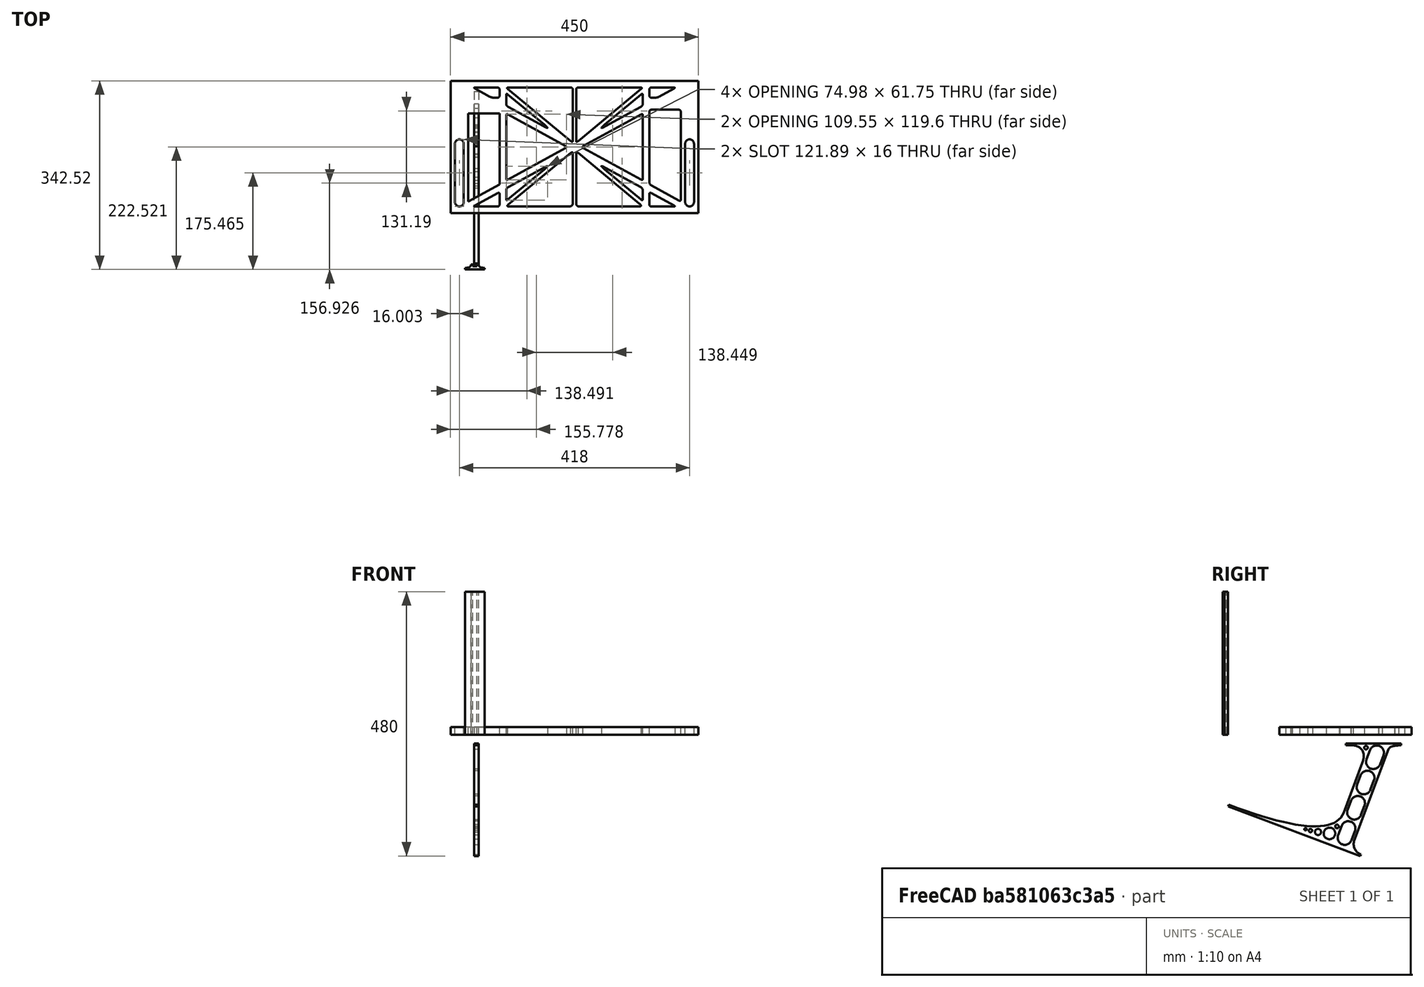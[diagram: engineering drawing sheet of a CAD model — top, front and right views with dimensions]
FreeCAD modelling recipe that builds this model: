
FCSTD DOCUMENT  (FreeCAD 0.19R0.19.2)
Label: laptopStand132FCStd
License: All rights reserved
LicenseURL: http://en.wikipedia.org/wiki/All_rights_reserved
objects: Sketcher::SketchObject×3, Part::Extrusion×3
note: 6 computed .brp shape members not serialized (recipe doc carries the construction recipe); baked Part::Feature solids carry a one-line shape summary decoded from their .brp

FEATURE [Sketcher::SketchObject] Sketch
  FullyConstrained = true
  sketch-geometry (351):
    g0: LineSegment StartX=-10.9272 StartY=-82.7794 StartZ=0 EndX=46.0728 EndY=-51.4823 EndZ=0
    g1: LineSegment StartX=-10.9272 StartY=76.4095 StartZ=0 EndX=-10.9272 EndY=-82.7794 EndZ=0
    g2: LineSegment StartX=46.0728 StartY=76.4095 StartZ=0 EndX=46.0728 EndY=-51.4823 EndZ=0
    g3: LineSegment StartX=-42.9272 StartY=136.221 StartZ=0 EndX=-42.9272 EndY=-103.779 EndZ=0
    g4: LineSegment StartX=407.073 StartY=136.221 StartZ=0 EndX=407.073 EndY=-103.779 EndZ=0
    g5: ArcOfCircle CenterX=-26.9272 CenterY=22.1087 CenterZ=0 NormalX=0 NormalY=0 NormalZ=1 AngleXU=0 Radius=8 StartAngle=1e-16 EndAngle=3.14159
    g6: ArcOfCircle CenterX=-26.9272 CenterY=-83.7794 CenterZ=0 NormalX=0 NormalY=0 NormalZ=1 AngleXU=0 Radius=8 StartAngle=3.14159 EndAngle=6.28319
    g7: LineSegment StartX=-34.9272 StartY=22.1087 StartZ=0 EndX=-34.9272 EndY=-83.7794 EndZ=0
    g8: LineSegment StartX=-18.9272 StartY=22.1087 StartZ=0 EndX=-18.9272 EndY=-83.7794 EndZ=0
    g9: ArcOfCircle CenterX=391.073 CenterY=22.1087 CenterZ=0 NormalX=0 NormalY=0 NormalZ=1 AngleXU=0 Radius=8 StartAngle=-4.4e-15 EndAngle=3.14159
    g10: LineSegment StartX=399.073 StartY=22.1087 StartZ=0 EndX=399.073 EndY=-83.7794 EndZ=0
    g11: LineSegment StartX=383.073 StartY=22.1087 StartZ=0 EndX=383.073 EndY=-83.7794 EndZ=0
    g12: ArcOfCircle CenterX=391.073 CenterY=-83.7794 CenterZ=0 NormalX=0 NormalY=0 NormalZ=1 AngleXU=0 Radius=8 StartAngle=3.14159 EndAngle=6.28319
    g13: Circle CenterX=175.022 CenterY=27.0628 CenterZ=0 NormalX=0 NormalY=0 NormalZ=1 AngleXU=0 Radius=1
    g14: Circle CenterX=179.022 CenterY=24.8665 CenterZ=0 NormalX=0 NormalY=0 NormalZ=1 AngleXU=0 Radius=1
    g15: Circle CenterX=179.022 CenterY=27.0628 CenterZ=0 NormalX=0 NormalY=0 NormalZ=1 AngleXU=0 Radius=1
    g16: BSplineCurve PolesCount=3 KnotsCount=2 Degree=2 IsPeriodic=0
    g17: GeomPoint X=175.022 Y=27.0628 Z=0
    g18: GeomPoint X=179.022 Y=27.0628 Z=0
    g19: Circle CenterX=189.124 CenterY=27.0628 CenterZ=0 NormalX=0 NormalY=0 NormalZ=1 AngleXU=0 Radius=1
    g20: Circle CenterX=185.124 CenterY=24.8665 CenterZ=0 NormalX=0 NormalY=0 NormalZ=1 AngleXU=0 Radius=1
    g21: Circle CenterX=185.124 CenterY=27.0628 CenterZ=0 NormalX=0 NormalY=0 NormalZ=1 AngleXU=0 Radius=1
    g22: BSplineCurve PolesCount=3 KnotsCount=2 Degree=2 IsPeriodic=0
    g23: GeomPoint X=189.124 Y=27.0628 Z=0
    g24: GeomPoint X=185.124 Y=27.0628 Z=0
    g25: Circle CenterX=175.022 CenterY=5.37834 CenterZ=0 NormalX=0 NormalY=0 NormalZ=1 AngleXU=0 Radius=1
    g26: Circle CenterX=179.022 CenterY=7.57463 CenterZ=0 NormalX=0 NormalY=0 NormalZ=1 AngleXU=0 Radius=1
    g27: Circle CenterX=179.022 CenterY=5.34704 CenterZ=0 NormalX=0 NormalY=0 NormalZ=1 AngleXU=0 Radius=1
    g28: BSplineCurve PolesCount=3 KnotsCount=2 Degree=2 IsPeriodic=0
    g29: GeomPoint X=175.022 Y=5.37834 Z=0
    g30: GeomPoint X=179.022 Y=5.34704 Z=0
    g31: Circle CenterX=189.124 CenterY=5.37834 CenterZ=0 NormalX=0 NormalY=0 NormalZ=1 AngleXU=0 Radius=1
    g32: Circle CenterX=185.124 CenterY=7.57463 CenterZ=0 NormalX=0 NormalY=0 NormalZ=1 AngleXU=0 Radius=1
    g33: Circle CenterX=185.124 CenterY=5.34704 CenterZ=0 NormalX=0 NormalY=0 NormalZ=1 AngleXU=0 Radius=1
    g34: BSplineCurve PolesCount=3 KnotsCount=2 Degree=2 IsPeriodic=0
    g35: GeomPoint X=189.124 Y=5.37834 Z=0
    g36: GeomPoint X=185.124 Y=5.34704 Z=0
    g37: Circle CenterX=165.871 CenterY=18.1458 CenterZ=0 NormalX=0 NormalY=0 NormalZ=1 AngleXU=0 Radius=1
    g38: Circle CenterX=169.377 CenterY=16.2206 CenterZ=0 NormalX=0 NormalY=0 NormalZ=1 AngleXU=0 Radius=1
    g39: Circle CenterX=165.871 CenterY=14.2954 CenterZ=0 NormalX=0 NormalY=0 NormalZ=1 AngleXU=0 Radius=1
    g40: BSplineCurve PolesCount=3 KnotsCount=2 Degree=2 IsPeriodic=0
    g41: GeomPoint X=165.871 Y=18.1458 Z=0
    g42: GeomPoint X=165.871 Y=14.2954 Z=0
    g43: Circle CenterX=198.275 CenterY=18.1458 CenterZ=0 NormalX=0 NormalY=0 NormalZ=1 AngleXU=0 Radius=1
    g44: Circle CenterX=194.768 CenterY=16.2206 CenterZ=0 NormalX=0 NormalY=0 NormalZ=1 AngleXU=0 Radius=1
    g45: Circle CenterX=198.275 CenterY=14.2954 CenterZ=0 NormalX=0 NormalY=0 NormalZ=1 AngleXU=0 Radius=1
    g46: BSplineCurve PolesCount=3 KnotsCount=2 Degree=2 IsPeriodic=0
    g47: GeomPoint X=198.275 Y=18.1458 Z=0
    g48: GeomPoint X=198.275 Y=14.2954 Z=0
    g49: LineSegment StartX=407.073 StartY=-103.779 StartZ=0 EndX=-42.9272 EndY=-103.779 EndZ=0
    g50: LineSegment StartX=407.073 StartY=136.221 StartZ=0 EndX=-42.9272 EndY=136.221 EndZ=0
    g51: LineSegment StartX=46.0728 StartY=76.4095 StartZ=0 EndX=-10.9272 EndY=76.4095 EndZ=0
    g52: Circle CenterX=125.607 CenterY=54.1951 CenterZ=0 NormalX=0 NormalY=0 NormalZ=1 AngleXU=0 Radius=1
    g53: Circle CenterX=139.632 CenterY=46.4944 CenterZ=0 NormalX=0 NormalY=0 NormalZ=1 AngleXU=0 Radius=1
    g54: Circle CenterX=127.326 CenterY=56.7187 CenterZ=0 NormalX=0 NormalY=0 NormalZ=1 AngleXU=0 Radius=1
    g55: BSplineCurve PolesCount=3 KnotsCount=2 Degree=2 IsPeriodic=0
    g56: GeomPoint X=125.607 Y=54.1951 Z=0
    g57: GeomPoint X=127.326 Y=56.7187 Z=0
    g58: Circle CenterX=236.821 CenterY=56.7187 CenterZ=0 NormalX=0 NormalY=0 NormalZ=1 AngleXU=0 Radius=1
    g59: Circle CenterX=224.513 CenterY=46.4944 CenterZ=0 NormalX=0 NormalY=0 NormalZ=1 AngleXU=0 Radius=1
    g60: Circle CenterX=238.538 CenterY=54.1951 CenterZ=0 NormalX=0 NormalY=0 NormalZ=1 AngleXU=0 Radius=1
    g61: BSplineCurve PolesCount=3 KnotsCount=2 Degree=2 IsPeriodic=0
    g62: GeomPoint X=236.821 Y=56.7187 Z=0
    g63: GeomPoint X=238.538 Y=54.1951 Z=0
    g64: Circle CenterX=238.538 CenterY=-21.7539 CenterZ=0 NormalX=0 NormalY=0 NormalZ=1 AngleXU=0 Radius=1
    g65: Circle CenterX=224.513 CenterY=-14.0532 CenterZ=0 NormalX=0 NormalY=0 NormalZ=1 AngleXU=0 Radius=1
    g66: Circle CenterX=236.821 CenterY=-24.2775 CenterZ=0 NormalX=0 NormalY=0 NormalZ=1 AngleXU=0 Radius=1
    g67: BSplineCurve PolesCount=3 KnotsCount=2 Degree=2 IsPeriodic=0
    g68: GeomPoint X=238.538 Y=-21.7539 Z=0
    g69: GeomPoint X=236.821 Y=-24.2775 Z=0
    g70: Circle CenterX=125.607 CenterY=-21.7539 CenterZ=0 NormalX=0 NormalY=0 NormalZ=1 AngleXU=0 Radius=1
    g71: Circle CenterX=139.632 CenterY=-14.0532 CenterZ=0 NormalX=0 NormalY=0 NormalZ=1 AngleXU=0 Radius=1
    g72: Circle CenterX=127.325 CenterY=-24.2775 CenterZ=0 NormalX=0 NormalY=0 NormalZ=1 AngleXU=0 Radius=1
    g73: BSplineCurve PolesCount=3 KnotsCount=2 Degree=2 IsPeriodic=0
    g74: GeomPoint X=125.607 Y=-21.7539 Z=0
    g75: GeomPoint X=127.325 Y=-24.2775 Z=0
    g76: Circle CenterX=302.996 CenterY=111.695 CenterZ=0 NormalX=0 NormalY=0 NormalZ=1 AngleXU=0 Radius=1
    g77: Circle CenterX=306.073 CenterY=114.251 CenterZ=0 NormalX=0 NormalY=0 NormalZ=1 AngleXU=0 Radius=1
    g78: Circle CenterX=306.073 CenterY=110.251 CenterZ=0 NormalX=0 NormalY=0 NormalZ=1 AngleXU=0 Radius=1
    g79: BSplineCurve PolesCount=3 KnotsCount=2 Degree=2 IsPeriodic=0
    g80: GeomPoint X=302.996 Y=111.695 Z=0
    g81: GeomPoint X=306.073 Y=110.251 Z=0
    g82: Circle CenterX=306.073 CenterY=95.2763 CenterZ=0 NormalX=0 NormalY=0 NormalZ=1 AngleXU=0 Radius=1
    g83: Circle CenterX=306.073 CenterY=91.2763 CenterZ=0 NormalX=0 NormalY=0 NormalZ=1 AngleXU=0 Radius=1
    g84: Circle CenterX=302.567 CenterY=89.3511 CenterZ=0 NormalX=0 NormalY=0 NormalZ=1 AngleXU=0 Radius=1
    g85: BSplineCurve PolesCount=3 KnotsCount=2 Degree=2 IsPeriodic=0
    g86: GeomPoint X=306.073 Y=95.2763 Z=0
    g87: GeomPoint X=302.567 Y=89.3511 Z=0
    g88: LineSegment StartX=306.073 StartY=110.251 StartZ=0 EndX=306.073 EndY=95.2763 EndZ=0
    g89: LineSegment StartX=302.996 StartY=111.695 StartZ=0 EndX=236.821 EndY=56.7187 EndZ=0
    g90: LineSegment StartX=238.538 StartY=54.1951 StartZ=0 EndX=302.567 EndY=89.3511 EndZ=0
    g91: Circle CenterX=61.1496 CenterY=111.695 CenterZ=0 NormalX=0 NormalY=0 NormalZ=1 AngleXU=0 Radius=1
    g92: Circle CenterX=58.0728 CenterY=114.251 CenterZ=0 NormalX=0 NormalY=0 NormalZ=1 AngleXU=0 Radius=1
    g93: Circle CenterX=58.0728 CenterY=110.251 CenterZ=0 NormalX=0 NormalY=0 NormalZ=1 AngleXU=0 Radius=1
    g94: BSplineCurve PolesCount=3 KnotsCount=2 Degree=2 IsPeriodic=0
    g95: GeomPoint X=61.1496 Y=111.695 Z=0
    g96: GeomPoint X=58.0728 Y=110.251 Z=0
    g97: Circle CenterX=61.5791 CenterY=89.3511 CenterZ=0 NormalX=0 NormalY=0 NormalZ=1 AngleXU=0 Radius=1
    g98: Circle CenterX=58.0728 CenterY=91.2763 CenterZ=0 NormalX=0 NormalY=0 NormalZ=1 AngleXU=0 Radius=1
    g99: Circle CenterX=58.0728 CenterY=95.2763 CenterZ=0 NormalX=0 NormalY=0 NormalZ=1 AngleXU=0 Radius=1
    g100: BSplineCurve PolesCount=3 KnotsCount=2 Degree=2 IsPeriodic=0
    g101: GeomPoint X=61.5791 Y=89.3511 Z=0
    g102: GeomPoint X=58.0728 Y=95.2763 Z=0
    g103: LineSegment StartX=58.0728 StartY=110.251 StartZ=0 EndX=58.0728 EndY=95.2763 EndZ=0
    g104: LineSegment StartX=61.1496 StartY=111.695 StartZ=0 EndX=127.326 EndY=56.7187 EndZ=0
    g105: LineSegment StartX=125.607 StartY=54.1951 StartZ=0 EndX=61.5791 EndY=89.3511 EndZ=0
    g106: Circle CenterX=61.5791 CenterY=-56.9099 CenterZ=0 NormalX=0 NormalY=0 NormalZ=1 AngleXU=0 Radius=1
    g107: Circle CenterX=58.0728 CenterY=-58.8351 CenterZ=0 NormalX=0 NormalY=0 NormalZ=1 AngleXU=0 Radius=1
    g108: Circle CenterX=58.0728 CenterY=-62.8351 CenterZ=0 NormalX=0 NormalY=0 NormalZ=1 AngleXU=0 Radius=1
    g109: BSplineCurve PolesCount=3 KnotsCount=2 Degree=2 IsPeriodic=0
    g110: GeomPoint X=61.5791 Y=-56.9099 Z=0
    g111: GeomPoint X=58.0728 Y=-62.8351 Z=0
    g112: Circle CenterX=58.0728 CenterY=-77.8102 CenterZ=0 NormalX=0 NormalY=0 NormalZ=1 AngleXU=0 Radius=1
    g113: Circle CenterX=58.0728 CenterY=-81.8102 CenterZ=0 NormalX=0 NormalY=0 NormalZ=1 AngleXU=0 Radius=1
    g114: Circle CenterX=61.1496 CenterY=-79.2541 CenterZ=0 NormalX=0 NormalY=0 NormalZ=1 AngleXU=0 Radius=1
    g115: BSplineCurve PolesCount=3 KnotsCount=2 Degree=2 IsPeriodic=0
    g116: GeomPoint X=58.0728 Y=-77.8102 Z=0
    g117: GeomPoint X=61.1496 Y=-79.2541 Z=0
    g118: LineSegment StartX=58.0728 StartY=-62.8351 StartZ=0 EndX=58.0728 EndY=-77.8102 EndZ=0
    g119: LineSegment StartX=61.1496 StartY=-79.2541 StartZ=0 EndX=127.325 EndY=-24.2775 EndZ=0
    g120: LineSegment StartX=125.607 StartY=-21.7539 StartZ=0 EndX=61.5791 EndY=-56.9099 EndZ=0
    g121: Circle CenterX=302.567 CenterY=-56.9099 CenterZ=0 NormalX=0 NormalY=0 NormalZ=1 AngleXU=0 Radius=1
    g122: Circle CenterX=306.073 CenterY=-58.8351 CenterZ=0 NormalX=0 NormalY=0 NormalZ=1 AngleXU=0 Radius=1
    g123: Circle CenterX=306.073 CenterY=-62.8351 CenterZ=0 NormalX=0 NormalY=0 NormalZ=1 AngleXU=0 Radius=1
    g124: BSplineCurve PolesCount=3 KnotsCount=2 Degree=2 IsPeriodic=0
    g125: GeomPoint X=302.567 Y=-56.9099 Z=0
    g126: GeomPoint X=306.073 Y=-62.8351 Z=0
    g127: Circle CenterX=302.996 CenterY=-79.2541 CenterZ=0 NormalX=0 NormalY=0 NormalZ=1 AngleXU=0 Radius=1
    g128: Circle CenterX=306.073 CenterY=-81.8102 CenterZ=0 NormalX=0 NormalY=0 NormalZ=1 AngleXU=0 Radius=1
    g129: Circle CenterX=306.073 CenterY=-77.8102 CenterZ=0 NormalX=0 NormalY=0 NormalZ=1 AngleXU=0 Radius=1
    g130: BSplineCurve PolesCount=3 KnotsCount=2 Degree=2 IsPeriodic=0
    g131: GeomPoint X=302.996 Y=-79.2541 Z=0
    g132: GeomPoint X=306.073 Y=-77.8102 Z=0
    g133: LineSegment StartX=306.073 StartY=-62.8351 StartZ=0 EndX=306.073 EndY=-77.8102 EndZ=0
    g134: LineSegment StartX=302.996 StartY=-79.2541 StartZ=0 EndX=236.821 EndY=-24.2775 EndZ=0
    g135: LineSegment StartX=238.538 StartY=-21.7539 StartZ=0 EndX=302.567 EndY=-56.9099 EndZ=0
    g136: Circle CenterX=61.6457 CenterY=-88.8112 CenterZ=0 NormalX=0 NormalY=0 NormalZ=1 AngleXU=0 Radius=1
    g137: Circle CenterX=58.0728 CenterY=-91.7794 CenterZ=0 NormalX=0 NormalY=0 NormalZ=1 AngleXU=0 Radius=1
    g138: Circle CenterX=63.9135 CenterY=-91.7794 CenterZ=0 NormalX=0 NormalY=0 NormalZ=1 AngleXU=0 Radius=1
    g139: BSplineCurve PolesCount=3 KnotsCount=2 Degree=2 IsPeriodic=0
    g140: GeomPoint X=61.6457 Y=-88.8112 Z=0
    g141: GeomPoint X=63.9135 Y=-91.7794 Z=0
    g142: Circle CenterX=179.022 CenterY=-85.8163 CenterZ=0 NormalX=0 NormalY=0 NormalZ=1 AngleXU=0 Radius=1
    g143: Circle CenterX=179.022 CenterY=-91.7794 CenterZ=0 NormalX=0 NormalY=0 NormalZ=1 AngleXU=0 Radius=1
    g144: Circle CenterX=171.895 CenterY=-91.7794 CenterZ=0 NormalX=0 NormalY=0 NormalZ=1 AngleXU=0 Radius=1
    g145: BSplineCurve PolesCount=3 KnotsCount=2 Degree=2 IsPeriodic=0
    g146: GeomPoint X=179.022 Y=-85.8163 Z=0
    g147: GeomPoint X=171.895 Y=-91.7794 Z=0
    g148: Circle CenterX=185.124 CenterY=-86.2028 CenterZ=0 NormalX=0 NormalY=0 NormalZ=1 AngleXU=0 Radius=1
    g149: Circle CenterX=185.124 CenterY=-91.7794 CenterZ=0 NormalX=0 NormalY=0 NormalZ=1 AngleXU=0 Radius=1
    g150: Circle CenterX=191.747 CenterY=-91.7794 CenterZ=0 NormalX=0 NormalY=0 NormalZ=1 AngleXU=0 Radius=1
    g151: BSplineCurve PolesCount=3 KnotsCount=2 Degree=2 IsPeriodic=0
    g152: GeomPoint X=185.124 Y=-86.2028 Z=0
    g153: GeomPoint X=191.747 Y=-91.7794 Z=0
    g154: Circle CenterX=299.888 CenterY=-86.6413 CenterZ=0 NormalX=0 NormalY=0 NormalZ=1 AngleXU=0 Radius=1
    g155: Circle CenterX=306.073 CenterY=-91.7794 CenterZ=0 NormalX=0 NormalY=0 NormalZ=1 AngleXU=0 Radius=1
    g156: Circle CenterX=298.776 CenterY=-91.7794 CenterZ=0 NormalX=0 NormalY=0 NormalZ=1 AngleXU=0 Radius=1
    g157: BSplineCurve PolesCount=3 KnotsCount=2 Degree=2 IsPeriodic=0
    g158: GeomPoint X=299.888 Y=-86.6413 Z=0
    g159: GeomPoint X=298.776 Y=-91.7794 Z=0
    g160: LineSegment StartX=189.124 StartY=5.37834 StartZ=0 EndX=299.888 EndY=-86.6413 EndZ=0
    g161: LineSegment StartX=298.776 StartY=-91.7794 StartZ=0 EndX=191.747 EndY=-91.7794 EndZ=0
    g162: LineSegment StartX=185.124 StartY=-86.2028 StartZ=0 EndX=185.124 EndY=5.34704 EndZ=0
    g163: LineSegment StartX=179.022 StartY=5.34704 StartZ=0 EndX=179.022 EndY=-85.8163 EndZ=0
    g164: LineSegment StartX=171.895 StartY=-91.7794 StartZ=0 EndX=63.9135 EndY=-91.7794 EndZ=0
    g165: LineSegment StartX=61.6457 StartY=-88.8112 StartZ=0 EndX=175.022 EndY=5.37834 EndZ=0
    g166: Circle CenterX=302.073 CenterY=124.221 CenterZ=0 NormalX=0 NormalY=0 NormalZ=1 AngleXU=0 Radius=1
    g167: Circle CenterX=306.073 CenterY=124.221 CenterZ=0 NormalX=0 NormalY=0 NormalZ=1 AngleXU=0 Radius=1
    g168: Circle CenterX=302.996 CenterY=121.665 CenterZ=0 NormalX=0 NormalY=0 NormalZ=1 AngleXU=0 Radius=1
    g169: BSplineCurve PolesCount=3 KnotsCount=2 Degree=2 IsPeriodic=0
    g170: GeomPoint X=302.073 Y=124.221 Z=0
    g171: GeomPoint X=302.996 Y=121.665 Z=0
    g172: Circle CenterX=189.124 CenterY=124.221 CenterZ=0 NormalX=0 NormalY=0 NormalZ=1 AngleXU=0 Radius=1
    g173: Circle CenterX=185.124 CenterY=124.221 CenterZ=0 NormalX=0 NormalY=0 NormalZ=1 AngleXU=0 Radius=1
    g174: Circle CenterX=185.124 CenterY=120.221 CenterZ=0 NormalX=0 NormalY=0 NormalZ=1 AngleXU=0 Radius=1
    g175: BSplineCurve PolesCount=3 KnotsCount=2 Degree=2 IsPeriodic=0
    g176: GeomPoint X=189.124 Y=124.221 Z=0
    g177: GeomPoint X=185.124 Y=120.221 Z=0
    g178: Circle CenterX=175.022 CenterY=124.221 CenterZ=0 NormalX=0 NormalY=0 NormalZ=1 AngleXU=0 Radius=1
    g179: Circle CenterX=179.022 CenterY=124.221 CenterZ=0 NormalX=0 NormalY=0 NormalZ=1 AngleXU=0 Radius=1
    g180: Circle CenterX=179.022 CenterY=120.221 CenterZ=0 NormalX=0 NormalY=0 NormalZ=1 AngleXU=0 Radius=1
    g181: BSplineCurve PolesCount=3 KnotsCount=2 Degree=2 IsPeriodic=0
    g182: GeomPoint X=175.022 Y=124.221 Z=0
    g183: GeomPoint X=179.022 Y=120.221 Z=0
    g184: Circle CenterX=62.0728 CenterY=124.221 CenterZ=0 NormalX=0 NormalY=0 NormalZ=1 AngleXU=0 Radius=1
    g185: Circle CenterX=58.0728 CenterY=124.221 CenterZ=0 NormalX=0 NormalY=0 NormalZ=1 AngleXU=0 Radius=1
    g186: Circle CenterX=61.1496 CenterY=121.665 CenterZ=0 NormalX=0 NormalY=0 NormalZ=1 AngleXU=0 Radius=1
    g187: BSplineCurve PolesCount=3 KnotsCount=2 Degree=2 IsPeriodic=0
    g188: GeomPoint X=62.0728 Y=124.221 Z=0
    g189: GeomPoint X=61.1496 Y=121.665 Z=0
    g190: LineSegment StartX=62.0728 StartY=124.221 StartZ=0 EndX=175.022 EndY=124.221 EndZ=0
    g191: LineSegment StartX=179.022 StartY=120.221 StartZ=0 EndX=179.022 EndY=27.0628 EndZ=0
    g192: LineSegment StartX=185.124 StartY=27.0628 StartZ=0 EndX=185.124 EndY=120.221 EndZ=0
    g193: LineSegment StartX=189.124 StartY=124.221 StartZ=0 EndX=302.073 EndY=124.221 EndZ=0
    g194: LineSegment StartX=302.996 StartY=121.665 StartZ=0 EndX=189.124 EndY=27.0628 EndZ=0
    g195: LineSegment StartX=175.022 StartY=27.0628 StartZ=0 EndX=61.1496 EndY=121.665 EndZ=0
    g196: Circle CenterX=61.5791 CenterY=75.4095 CenterZ=0 NormalX=0 NormalY=0 NormalZ=1 AngleXU=0 Radius=1
    g197: Circle CenterX=58.0728 CenterY=77.3346 CenterZ=0 NormalX=0 NormalY=0 NormalZ=1 AngleXU=0 Radius=1
    g198: Circle CenterX=58.0728 CenterY=73.3346 CenterZ=0 NormalX=0 NormalY=0 NormalZ=1 AngleXU=0 Radius=1
    g199: BSplineCurve PolesCount=3 KnotsCount=2 Degree=2 IsPeriodic=0
    g200: GeomPoint X=61.5791 Y=75.4095 Z=0
    g201: GeomPoint X=58.0728 Y=73.3346 Z=0
    g202: Circle CenterX=58.0728 CenterY=-40.8935 CenterZ=0 NormalX=0 NormalY=0 NormalZ=1 AngleXU=0 Radius=1
    g203: Circle CenterX=58.0728 CenterY=-44.8935 CenterZ=0 NormalX=0 NormalY=0 NormalZ=1 AngleXU=0 Radius=1
    g204: Circle CenterX=61.5791 CenterY=-42.9683 CenterZ=0 NormalX=0 NormalY=0 NormalZ=1 AngleXU=0 Radius=1
    g205: BSplineCurve PolesCount=3 KnotsCount=2 Degree=2 IsPeriodic=0
    g206: GeomPoint X=58.0728 Y=-40.8935 Z=0
    g207: GeomPoint X=61.5791 Y=-42.9683 Z=0
    g208: LineSegment StartX=61.5791 StartY=-42.9683 StartZ=0 EndX=165.871 EndY=14.2954 EndZ=0
    g209: LineSegment StartX=165.871 StartY=18.1458 StartZ=0 EndX=61.5791 EndY=75.4095 EndZ=0
    g210: LineSegment StartX=58.0728 StartY=73.3346 StartZ=0 EndX=58.0728 EndY=-40.8935 EndZ=0
    g211: Circle CenterX=302.567 CenterY=-42.9683 CenterZ=0 NormalX=0 NormalY=0 NormalZ=1 AngleXU=0 Radius=1
    g212: Circle CenterX=306.073 CenterY=-44.8935 CenterZ=0 NormalX=0 NormalY=0 NormalZ=1 AngleXU=0 Radius=1
    g213: Circle CenterX=306.073 CenterY=-40.8935 CenterZ=0 NormalX=0 NormalY=0 NormalZ=1 AngleXU=0 Radius=1
    g214: BSplineCurve PolesCount=3 KnotsCount=2 Degree=2 IsPeriodic=0
    g215: GeomPoint X=302.567 Y=-42.9683 Z=0
    g216: GeomPoint X=306.073 Y=-40.8935 Z=0
    g217: Circle CenterX=306.073 CenterY=73.3346 CenterZ=0 NormalX=0 NormalY=0 NormalZ=1 AngleXU=0 Radius=1
    g218: Circle CenterX=306.073 CenterY=77.3346 CenterZ=0 NormalX=0 NormalY=0 NormalZ=1 AngleXU=0 Radius=1
    g219: Circle CenterX=302.567 CenterY=75.4095 CenterZ=0 NormalX=0 NormalY=0 NormalZ=1 AngleXU=0 Radius=1
    g220: BSplineCurve PolesCount=3 KnotsCount=2 Degree=2 IsPeriodic=0
    g221: GeomPoint X=306.073 Y=73.3346 Z=0
    g222: GeomPoint X=302.567 Y=75.4095 Z=0
    g223: LineSegment StartX=302.567 StartY=-42.9683 StartZ=0 EndX=198.275 EndY=14.2954 EndZ=0
    g224: LineSegment StartX=198.275 StartY=18.1458 StartZ=0 EndX=302.567 EndY=75.4095 EndZ=0
    g225: LineSegment StartX=306.073 StartY=73.3346 StartZ=0 EndX=306.073 EndY=-40.8935 EndZ=0
    g226: LineSegment StartX=322.073 StartY=105.865 StartZ=0 EndX=328.643 EndY=105.865 EndZ=0
    g227: LineSegment StartX=318.073 StartY=120.221 StartZ=0 EndX=318.073 EndY=109.865 EndZ=0
    g228: LineSegment StartX=336.157 StartY=107.779 StartZ=0 EndX=362.567 EndY=122.294 EndZ=0
    g229: Circle CenterX=362.073 CenterY=124.221 CenterZ=0 NormalX=0 NormalY=0 NormalZ=1 AngleXU=0 Radius=1
    g230: Circle CenterX=366.073 CenterY=124.221 CenterZ=0 NormalX=0 NormalY=0 NormalZ=1 AngleXU=0 Radius=1
    g231: Circle CenterX=362.567 CenterY=122.294 CenterZ=0 NormalX=0 NormalY=0 NormalZ=1 AngleXU=0 Radius=1
    g232: BSplineCurve PolesCount=3 KnotsCount=2 Degree=2 IsPeriodic=0
    g233: GeomPoint X=362.073 Y=124.221 Z=0
    g234: GeomPoint X=362.567 Y=122.294 Z=0
    g235: Circle CenterX=322.073 CenterY=124.221 CenterZ=0 NormalX=0 NormalY=0 NormalZ=1 AngleXU=0 Radius=1
    g236: Circle CenterX=318.073 CenterY=124.221 CenterZ=0 NormalX=0 NormalY=0 NormalZ=1 AngleXU=0 Radius=1
    g237: Circle CenterX=318.073 CenterY=120.221 CenterZ=0 NormalX=0 NormalY=0 NormalZ=1 AngleXU=0 Radius=1
    g238: BSplineCurve PolesCount=3 KnotsCount=2 Degree=2 IsPeriodic=0
    g239: GeomPoint X=322.073 Y=124.221 Z=0
    g240: GeomPoint X=318.073 Y=120.221 Z=0
    g241: Circle CenterX=322.073 CenterY=105.865 CenterZ=0 NormalX=0 NormalY=0 NormalZ=1 AngleXU=0 Radius=1
    g242: Circle CenterX=318.073 CenterY=105.865 CenterZ=0 NormalX=0 NormalY=0 NormalZ=1 AngleXU=0 Radius=1
    g243: Circle CenterX=318.073 CenterY=109.865 CenterZ=0 NormalX=0 NormalY=0 NormalZ=1 AngleXU=0 Radius=1
    g244: BSplineCurve PolesCount=3 KnotsCount=2 Degree=2 IsPeriodic=0
    g245: GeomPoint X=322.073 Y=105.865 Z=0
    g246: GeomPoint X=318.073 Y=109.865 Z=0
    g247: Circle CenterX=336.157 CenterY=107.779 CenterZ=0 NormalX=0 NormalY=0 NormalZ=1 AngleXU=0 Radius=1
    g248: Circle CenterX=332.651 CenterY=105.853 CenterZ=0 NormalX=0 NormalY=0 NormalZ=1 AngleXU=0 Radius=1
    g249: Circle CenterX=328.643 CenterY=105.865 CenterZ=0 NormalX=0 NormalY=0 NormalZ=1 AngleXU=0 Radius=1
    g250: BSplineCurve PolesCount=3 KnotsCount=2 Degree=2 IsPeriodic=0
    g251: GeomPoint X=336.157 Y=107.779 Z=0
    g252: GeomPoint X=328.643 Y=105.865 Z=0
    g253: LineSegment StartX=322.073 StartY=124.221 StartZ=0 EndX=362.073 EndY=124.221 EndZ=0
    g254: Circle CenterX=371.567 CenterY=-80.8644 CenterZ=0 NormalX=0 NormalY=0 NormalZ=1 AngleXU=0 Radius=1
    g255: Circle CenterX=375.073 CenterY=-82.7896 CenterZ=0 NormalX=0 NormalY=0 NormalZ=1 AngleXU=0 Radius=1
    g256: Circle CenterX=375.073 CenterY=-78.7896 CenterZ=0 NormalX=0 NormalY=0 NormalZ=1 AngleXU=0 Radius=1
    g257: BSplineCurve PolesCount=3 KnotsCount=2 Degree=2 IsPeriodic=0
    g258: GeomPoint X=371.567 Y=-80.8644 Z=0
    g259: GeomPoint X=375.073 Y=-78.7896 Z=0
    g260: Circle CenterX=321.579 CenterY=-53.4075 CenterZ=0 NormalX=0 NormalY=0 NormalZ=1 AngleXU=0 Radius=1
    g261: Circle CenterX=318.073 CenterY=-51.4823 CenterZ=0 NormalX=0 NormalY=0 NormalZ=1 AngleXU=0 Radius=1
    g262: Circle CenterX=318.073 CenterY=-47.4823 CenterZ=0 NormalX=0 NormalY=0 NormalZ=1 AngleXU=0 Radius=1
    g263: BSplineCurve PolesCount=3 KnotsCount=2 Degree=2 IsPeriodic=0
    g264: GeomPoint X=321.579 Y=-53.4075 Z=0
    g265: GeomPoint X=318.073 Y=-47.4823 Z=0
    g266: LineSegment StartX=371.567 StartY=-80.8644 StartZ=0 EndX=321.579 EndY=-53.4075 EndZ=0
    g267: LineSegment StartX=318.073 StartY=-47.4823 StartZ=0 EndX=318.073 EndY=76.4095 EndZ=0
    g268: Circle CenterX=321.579 CenterY=-67.3492 CenterZ=0 NormalX=0 NormalY=0 NormalZ=1 AngleXU=0 Radius=1
    g269: Circle CenterX=318.073 CenterY=-65.424 CenterZ=0 NormalX=0 NormalY=0 NormalZ=1 AngleXU=0 Radius=1
    g270: Circle CenterX=318.073 CenterY=-69.424 CenterZ=0 NormalX=0 NormalY=0 NormalZ=1 AngleXU=0 Radius=1
    g271: BSplineCurve PolesCount=3 KnotsCount=2 Degree=2 IsPeriodic=0
    g272: GeomPoint X=321.579 Y=-67.3492 Z=0
    g273: GeomPoint X=318.073 Y=-69.424 Z=0
    g274: Circle CenterX=362.567 CenterY=-89.8542 CenterZ=0 NormalX=0 NormalY=0 NormalZ=1 AngleXU=0 Radius=1
    g275: Circle CenterX=366.073 CenterY=-91.7794 CenterZ=0 NormalX=0 NormalY=0 NormalZ=1 AngleXU=0 Radius=1
    g276: Circle CenterX=362.073 CenterY=-91.7794 CenterZ=0 NormalX=0 NormalY=0 NormalZ=1 AngleXU=0 Radius=1
    g277: BSplineCurve PolesCount=3 KnotsCount=2 Degree=2 IsPeriodic=0
    g278: GeomPoint X=362.567 Y=-89.8542 Z=0
    g279: GeomPoint X=362.073 Y=-91.7794 Z=0
    g280: Circle CenterX=322.073 CenterY=-91.7794 CenterZ=0 NormalX=0 NormalY=0 NormalZ=1 AngleXU=0 Radius=1
    g281: Circle CenterX=318.073 CenterY=-91.7794 CenterZ=0 NormalX=0 NormalY=0 NormalZ=1 AngleXU=0 Radius=1
    g282: Circle CenterX=318.073 CenterY=-87.7794 CenterZ=0 NormalX=0 NormalY=0 NormalZ=1 AngleXU=0 Radius=1
    g283: BSplineCurve PolesCount=3 KnotsCount=2 Degree=2 IsPeriodic=0
    g284: GeomPoint X=322.073 Y=-91.7794 Z=0
    g285: GeomPoint X=318.073 Y=-87.7794 Z=0
    g286: LineSegment StartX=362.567 StartY=-89.8542 StartZ=0 EndX=321.579 EndY=-67.3492 EndZ=0
    g287: LineSegment StartX=318.073 StartY=-69.424 StartZ=0 EndX=318.073 EndY=-87.7794 EndZ=0
    g288: LineSegment StartX=322.073 StartY=-91.7794 StartZ=0 EndX=362.073 EndY=-91.7794 EndZ=0
    g289: Circle CenterX=2.07281 CenterY=124.221 CenterZ=0 NormalX=0 NormalY=0 NormalZ=1 AngleXU=0 Radius=1
    g290: Circle CenterX=1.57905 CenterY=122.295 CenterZ=0 NormalX=0 NormalY=0 NormalZ=1 AngleXU=0 Radius=1
    g291: BSplineCurve PolesCount=3 KnotsCount=2 Degree=2 IsPeriodic=0
    g292: GeomPoint X=2.07281 Y=124.221 Z=0
    g293: GeomPoint X=1.57905 Y=122.295 Z=0
    g294: Circle CenterX=42.0728 CenterY=124.221 CenterZ=0 NormalX=0 NormalY=0 NormalZ=1 AngleXU=0 Radius=1
    g295: Circle CenterX=46.0728 CenterY=124.221 CenterZ=0 NormalX=0 NormalY=0 NormalZ=1 AngleXU=0 Radius=1
    g296: Circle CenterX=46.0728 CenterY=120.221 CenterZ=0 NormalX=0 NormalY=0 NormalZ=1 AngleXU=0 Radius=1
    g297: BSplineCurve PolesCount=3 KnotsCount=2 Degree=2 IsPeriodic=0
    g298: GeomPoint X=42.0728 Y=124.221 Z=0
    g299: GeomPoint X=46.0728 Y=120.221 Z=0
    g300: Circle CenterX=46.0728 CenterY=109.865 CenterZ=0 NormalX=0 NormalY=0 NormalZ=1 AngleXU=0 Radius=1
    g301: Circle CenterX=46.0728 CenterY=105.865 CenterZ=0 NormalX=0 NormalY=0 NormalZ=1 AngleXU=0 Radius=1
    g302: Circle CenterX=42.0728 CenterY=105.865 CenterZ=0 NormalX=0 NormalY=0 NormalZ=1 AngleXU=0 Radius=1
    g303: BSplineCurve PolesCount=3 KnotsCount=2 Degree=2 IsPeriodic=0
    g304: GeomPoint X=46.0728 Y=109.865 Z=0
    g305: GeomPoint X=42.0728 Y=105.865 Z=0
    g306: Circle CenterX=35.5028 CenterY=105.865 CenterZ=0 NormalX=0 NormalY=0 NormalZ=1 AngleXU=0 Radius=1
    g307: Circle CenterX=31.5028 CenterY=105.865 CenterZ=0 NormalX=0 NormalY=0 NormalZ=1 AngleXU=0 Radius=1
    g308: Circle CenterX=27.9965 CenterY=107.79 CenterZ=0 NormalX=0 NormalY=0 NormalZ=1 AngleXU=0 Radius=1
    g309: BSplineCurve PolesCount=3 KnotsCount=2 Degree=2 IsPeriodic=0
    g310: GeomPoint X=35.5028 Y=105.865 Z=0
    g311: GeomPoint X=27.9965 Y=107.79 Z=0
    g312: LineSegment StartX=2.07281 StartY=124.221 StartZ=0 EndX=42.0728 EndY=124.221 EndZ=0
    g313: LineSegment StartX=46.0728 StartY=120.221 StartZ=0 EndX=46.0728 EndY=109.865 EndZ=0
    g314: LineSegment StartX=42.0728 StartY=105.865 StartZ=0 EndX=35.5028 EndY=105.865 EndZ=0
    g315: LineSegment StartX=27.9965 StartY=107.79 StartZ=0 EndX=1.57905 EndY=122.295 EndZ=0
    g316: Circle CenterX=42.5666 CenterY=-67.3492 CenterZ=0 NormalX=0 NormalY=0 NormalZ=1 AngleXU=0 Radius=1
    g317: Circle CenterX=46.0728 CenterY=-65.424 CenterZ=0 NormalX=0 NormalY=0 NormalZ=1 AngleXU=0 Radius=1
    g318: Circle CenterX=46.0728 CenterY=-69.424 CenterZ=0 NormalX=0 NormalY=0 NormalZ=1 AngleXU=0 Radius=1
    g319: BSplineCurve PolesCount=3 KnotsCount=2 Degree=2 IsPeriodic=0
    g320: GeomPoint X=42.5666 Y=-67.3492 Z=0
    g321: GeomPoint X=46.0728 Y=-69.424 Z=0
    g322: Circle CenterX=46.0728 CenterY=-87.7794 CenterZ=0 NormalX=0 NormalY=0 NormalZ=1 AngleXU=0 Radius=1
    g323: Circle CenterX=46.0728 CenterY=-91.7794 CenterZ=0 NormalX=0 NormalY=0 NormalZ=1 AngleXU=0 Radius=1
    g324: Circle CenterX=42.0728 CenterY=-91.7794 CenterZ=0 NormalX=0 NormalY=0 NormalZ=1 AngleXU=0 Radius=1
    g325: BSplineCurve PolesCount=3 KnotsCount=2 Degree=2 IsPeriodic=0
    g326: GeomPoint X=46.0728 Y=-87.7794 Z=0
    g327: GeomPoint X=42.0728 Y=-91.7794 Z=0
    g328: Circle CenterX=2.07281 CenterY=-91.7794 CenterZ=0 NormalX=0 NormalY=0 NormalZ=1 AngleXU=0 Radius=1
    g329: Circle CenterX=-1.92719 CenterY=-91.7794 CenterZ=0 NormalX=0 NormalY=0 NormalZ=1 AngleXU=0 Radius=1
    g330: Circle CenterX=1.57905 CenterY=-89.8542 CenterZ=0 NormalX=0 NormalY=0 NormalZ=1 AngleXU=0 Radius=1
    g331: BSplineCurve PolesCount=3 KnotsCount=2 Degree=2 IsPeriodic=0
    g332: GeomPoint X=2.07281 Y=-91.7794 Z=0
    g333: GeomPoint X=1.57905 Y=-89.8542 Z=0
    g334: LineSegment StartX=2.07281 StartY=-91.7794 StartZ=0 EndX=42.0728 EndY=-91.7794 EndZ=0
    g335: LineSegment StartX=46.0728 StartY=-87.7794 StartZ=0 EndX=46.0728 EndY=-69.424 EndZ=0
    g336: LineSegment StartX=42.5666 StartY=-67.3492 StartZ=0 EndX=1.57905 EndY=-89.8542 EndZ=0
    g337: LineSegment StartX=318.073 StartY=76.4095 StartZ=0 EndX=375.073 EndY=76.4095 EndZ=0
    g338: LineSegment StartX=375.073 StartY=76.4095 StartZ=0 EndX=375.073 EndY=-78.7896 EndZ=0
    g339: LineSegment StartX=318.073 StartY=76.4095 StartZ=0 EndX=322.073 EndY=76.4095 EndZ=0
    g340: Circle CenterX=322.073 CenterY=76.4095 CenterZ=0 NormalX=0 NormalY=0 NormalZ=1 AngleXU=0 Radius=1
    g341: BSplineCurve PolesCount=3 KnotsCount=2 Degree=2 IsPeriodic=0
    g342: GeomPoint X=318.073 Y=72.4095 Z=0
    g343: GeomPoint X=322.073 Y=76.4095 Z=0
    g344: LineSegment StartX=371.073 StartY=76.4095 StartZ=0 EndX=375.073 EndY=76.4095 EndZ=0
    g345: Circle CenterX=375.073 CenterY=72.4095 CenterZ=0 NormalX=0 NormalY=0 NormalZ=1 AngleXU=0 Radius=1
    g346: Circle CenterX=375.073 CenterY=76.4095 CenterZ=0 NormalX=0 NormalY=0 NormalZ=1 AngleXU=0 Radius=1
    g347: Circle CenterX=371.073 CenterY=76.4095 CenterZ=0 NormalX=0 NormalY=0 NormalZ=1 AngleXU=0 Radius=1
    g348: BSplineCurve PolesCount=3 KnotsCount=2 Degree=2 IsPeriodic=0
    g349: GeomPoint X=375.073 Y=72.4095 Z=0
    g350: GeomPoint X=371.073 Y=76.4095 Z=0
  constraints (581):
    c: Coincident(g0,g2)
    c: Block(g0)
    c: Block(g1)
    c: Vertical(g3)
    c: Vertical(g4)
    c: Block(g4)
    c: Block(g3)
    c: Tangent(g5,g8) = 1.5708
    c: Tangent(g5,g7) = -1.5708
    c: Tangent(g7,g6) = -1.5708
    c: Tangent(g8,g6) = 1.5708
    c: Vertical(g7)
    c: Equal(g5,g6)
    c: Block(g8)
    c: Block(g7)
    c: Tangent(g9,g10) = 1.5708
    c: Tangent(g10,g12) = 1.5708
    c: Equal(g9,g12)
    c: Coincident(g11,g9)
    c: Coincident(g11,g12)
    c: Block(g10)
    c: Block(g11)
    c: Weight(g13) = 1
    c: Equal(g13,g14)
    c: Equal(g13,g15)
    c: InternalAlignment(g13,g16)
    c: InternalAlignment(g14,g16)
    c: InternalAlignment(g15,g16)
    c: InternalAlignment(g17,g16)
    c: InternalAlignment(g18,g16)
    c: Weight(g19) = 1
    c: Equal(g19,g20)
    c: Equal(g19,g21)
    c: InternalAlignment(g19,g22)
    c: InternalAlignment(g20,g22)
    c: InternalAlignment(g21,g22)
    c: InternalAlignment(g23,g22)
    c: InternalAlignment(g24,g22)
    c: Block(g22)
    c: Block(g16)
    c: Weight(g25) = 1
    c: Equal(g25,g26)
    c: Equal(g25,g27)
    c: InternalAlignment(g25,g28)
    c: InternalAlignment(g26,g28)
    c: InternalAlignment(g27,g28)
    c: InternalAlignment(g29,g28)
    c: InternalAlignment(g30,g28)
    c: Weight(g31) = 1
    c: Equal(g31,g32)
    c: Equal(g31,g33)
    c: InternalAlignment(g31,g34)
    c: InternalAlignment(g32,g34)
    c: InternalAlignment(g33,g34)
    c: InternalAlignment(g35,g34)
    c: InternalAlignment(g36,g34)
    c: Block(g34)
    c: Block(g28)
    c: Weight(g37) = 1
    c: Equal(g37,g38)
    c: Equal(g37,g39)
    c: InternalAlignment(g37,g40)
    c: InternalAlignment(g38,g40)
    c: InternalAlignment(g39,g40)
    c: InternalAlignment(g41,g40)
    c: InternalAlignment(g42,g40)
    c: Weight(g43) = 1
    c: Equal(g43,g44)
    c: Equal(g43,g45)
    c: InternalAlignment(g43,g46)
    c: InternalAlignment(g44,g46)
    c: InternalAlignment(g45,g46)
    c: InternalAlignment(g47,g46)
    c: InternalAlignment(g48,g46)
    c: Block(g40)
    c: Block(g46)
    c: Coincident(g49,g4)
    c: Coincident(g49,g3)
    c: Horizontal(g49)
    c: Distance(g49) = 450
    c: Coincident(g50,g4)
    c: Coincident(g50,g3)
    c: Horizontal(g50)
    c: Horizontal(g51)
    c: Coincident(g2,g51)
    c: Block(g51)
    c: Coincident(g1,g51)
    c: Weight(g52) = 1
    c: Equal(g52,g53)
    c: Equal(g52,g54)
    c: InternalAlignment(g52,g55)
    c: InternalAlignment(g53,g55)
    c: InternalAlignment(g54,g55)
    c: InternalAlignment(g56,g55)
    c: InternalAlignment(g57,g55)
    c: Block(g55)
    c: Weight(g58) = 1
    c: Equal(g58,g59)
    c: Equal(g58,g60)
    c: InternalAlignment(g58,g61)
    c: InternalAlignment(g59,g61)
    c: InternalAlignment(g60,g61)
    c: InternalAlignment(g62,g61)
    c: InternalAlignment(g63,g61)
    c: Block(g61)
    c: Weight(g64) = 1
    c: Equal(g64,g65)
    c: Equal(g64,g66)
    c: InternalAlignment(g64,g67)
    c: InternalAlignment(g65,g67)
    c: InternalAlignment(g66,g67)
    c: InternalAlignment(g68,g67)
    c: InternalAlignment(g69,g67)
    c: Block(g67)
    c: Weight(g70) = 1
    c: Equal(g70,g71)
    c: Equal(g70,g72)
    c: InternalAlignment(g70,g73)
    c: InternalAlignment(g71,g73)
    c: InternalAlignment(g72,g73)
    c: InternalAlignment(g74,g73)
    c: InternalAlignment(g75,g73)
    c: Block(g73)
    c: Weight(g76) = 1
    c: Equal(g76,g77)
    c: Equal(g76,g78)
    c: InternalAlignment(g76,g79)
    c: InternalAlignment(g77,g79)
    c: InternalAlignment(g78,g79)
    c: InternalAlignment(g80,g79)
    c: InternalAlignment(g81,g79)
    c: Weight(g82) = 1
    c: Equal(g82,g83)
    c: Equal(g82,g84)
    c: InternalAlignment(g82,g85)
    c: InternalAlignment(g83,g85)
    c: InternalAlignment(g84,g85)
    c: InternalAlignment(g86,g85)
    c: InternalAlignment(g87,g85)
    c: Block(g79)
    c: Block(g85)
    c: Coincident(g88,g79)
    c: Coincident(g88,g85)
    c: Vertical(g88)
    c: Coincident(g89,g79)
    c: Coincident(g89,g61)
    c: Coincident(g90,g61)
    c: Coincident(g90,g85)
    c: Weight(g91) = 1
    c: Equal(g91,g92)
    c: Equal(g91,g93)
    c: InternalAlignment(g91,g94)
    c: InternalAlignment(g92,g94)
    c: InternalAlignment(g93,g94)
    c: InternalAlignment(g95,g94)
    c: InternalAlignment(g96,g94)
    c: Weight(g97) = 1
    c: Equal(g97,g98)
    c: Equal(g97,g99)
    c: InternalAlignment(g97,g100)
    c: InternalAlignment(g98,g100)
    c: InternalAlignment(g99,g100)
    c: InternalAlignment(g101,g100)
    c: InternalAlignment(g102,g100)
    c: Block(g94)
    c: Block(g100)
    c: Coincident(g103,g94)
    c: Coincident(g103,g100)
    c: Vertical(g103)
    c: Coincident(g104,g94)
    c: Coincident(g104,g55)
    c: Coincident(g105,g55)
    c: Coincident(g105,g100)
    c: Weight(g106) = 1
    c: Equal(g106,g107)
    c: Equal(g106,g108)
    c: InternalAlignment(g106,g109)
    c: InternalAlignment(g107,g109)
    c: InternalAlignment(g108,g109)
    c: InternalAlignment(g110,g109)
    c: InternalAlignment(g111,g109)
    c: Weight(g112) = 1
    c: Equal(g112,g113)
    c: Equal(g112,g114)
    c: InternalAlignment(g112,g115)
    c: InternalAlignment(g113,g115)
    c: InternalAlignment(g114,g115)
    c: InternalAlignment(g116,g115)
    c: InternalAlignment(g117,g115)
    c: Block(g109)
    c: Block(g115)
    c: Coincident(g118,g109)
    c: Coincident(g118,g115)
    c: Vertical(g118)
    c: Coincident(g119,g115)
    c: Coincident(g119,g73)
    c: Coincident(g120,g73)
    c: Coincident(g120,g109)
    c: Weight(g121) = 1
    c: Equal(g121,g122)
    c: Equal(g121,g123)
    c: InternalAlignment(g121,g124)
    c: InternalAlignment(g122,g124)
    c: InternalAlignment(g123,g124)
    c: InternalAlignment(g125,g124)
    c: InternalAlignment(g126,g124)
    c: Weight(g127) = 1
    c: Equal(g127,g128)
    c: Equal(g127,g129)
    c: InternalAlignment(g127,g130)
    c: InternalAlignment(g128,g130)
    c: InternalAlignment(g129,g130)
    c: InternalAlignment(g131,g130)
    c: InternalAlignment(g132,g130)
    c: Block(g124)
    c: Block(g130)
    c: Coincident(g133,g124)
    c: Coincident(g133,g130)
    c: Vertical(g133)
    c: Coincident(g134,g130)
    c: Coincident(g134,g67)
    c: Coincident(g135,g67)
    c: Coincident(g135,g124)
    c: Weight(g136) = 1
    c: Equal(g136,g137)
    c: Equal(g136,g138)
    c: InternalAlignment(g136,g139)
    c: InternalAlignment(g137,g139)
    c: InternalAlignment(g138,g139)
    c: InternalAlignment(g140,g139)
    c: InternalAlignment(g141,g139)
    c: Weight(g142) = 1
    c: Equal(g142,g143)
    c: Equal(g142,g144)
    c: InternalAlignment(g142,g145)
    c: InternalAlignment(g143,g145)
    c: InternalAlignment(g144,g145)
    c: InternalAlignment(g146,g145)
    c: InternalAlignment(g147,g145)
    c: Weight(g148) = 1
    c: Equal(g148,g149)
    c: Equal(g148,g150)
    c: InternalAlignment(g148,g151)
    c: InternalAlignment(g149,g151)
    c: InternalAlignment(g150,g151)
    c: InternalAlignment(g152,g151)
    c: InternalAlignment(g153,g151)
    c: Weight(g154) = 1
    c: Equal(g154,g155)
    c: Equal(g154,g156)
    c: InternalAlignment(g154,g157)
    c: InternalAlignment(g155,g157)
    c: InternalAlignment(g156,g157)
    c: InternalAlignment(g158,g157)
    c: InternalAlignment(g159,g157)
    c: Block(g157)
    c: Block(g151)
    c: Block(g145)
    c: Block(g139)
    c: Coincident(g160,g34)
    c: Coincident(g160,g157)
    c: Coincident(g161,g157)
    c: Coincident(g161,g151)
    c: Horizontal(g161)
    c: Coincident(g162,g151)
    c: Coincident(g162,g34)
    c: Vertical(g162)
    c: Coincident(g163,g28)
    c: Coincident(g163,g145)
    c: Vertical(g163)
    c: Coincident(g164,g145)
    c: Coincident(g164,g139)
    c: Horizontal(g164)
    c: Coincident(g165,g139)
    c: Coincident(g165,g28)
    c: Weight(g166) = 1
    c: Equal(g166,g167)
    c: Equal(g166,g168)
    c: InternalAlignment(g166,g169)
    c: InternalAlignment(g167,g169)
    c: InternalAlignment(g168,g169)
    c: InternalAlignment(g170,g169)
    c: InternalAlignment(g171,g169)
    c: Weight(g172) = 1
    c: Equal(g172,g173)
    c: Equal(g172,g174)
    c: InternalAlignment(g172,g175)
    c: InternalAlignment(g173,g175)
    c: InternalAlignment(g174,g175)
    c: InternalAlignment(g176,g175)
    c: InternalAlignment(g177,g175)
    c: Weight(g178) = 1
    c: Equal(g178,g179)
    c: Equal(g178,g180)
    c: InternalAlignment(g178,g181)
    c: InternalAlignment(g179,g181)
    c: InternalAlignment(g180,g181)
    c: InternalAlignment(g182,g181)
    c: InternalAlignment(g183,g181)
    c: Weight(g184) = 1
    c: Equal(g184,g185)
    c: Equal(g184,g186)
    c: InternalAlignment(g184,g187)
    c: InternalAlignment(g185,g187)
    c: InternalAlignment(g186,g187)
    c: InternalAlignment(g188,g187)
    c: InternalAlignment(g189,g187)
    c: Block(g187)
    c: Block(g181)
    c: Block(g175)
    c: Block(g169)
    c: Coincident(g190,g187)
    c: Coincident(g190,g181)
    c: Horizontal(g190)
    c: Coincident(g191,g181)
    c: Coincident(g191,g16)
    c: Vertical(g191)
    c: Coincident(g192,g22)
    c: Coincident(g192,g175)
    c: Vertical(g192)
    c: Coincident(g193,g175)
    c: Coincident(g193,g169)
    c: Horizontal(g193)
    c: Coincident(g194,g169)
    c: Coincident(g194,g22)
    c: Coincident(g195,g16)
    c: Weight(g196) = 1
    c: Equal(g196,g197)
    c: Equal(g196,g198)
    c: InternalAlignment(g196,g199)
    c: InternalAlignment(g197,g199)
    c: InternalAlignment(g198,g199)
    c: InternalAlignment(g200,g199)
    c: InternalAlignment(g201,g199)
    c: Weight(g202) = 1
    c: Equal(g202,g203)
    c: Equal(g202,g204)
    c: InternalAlignment(g202,g205)
    c: InternalAlignment(g203,g205)
    c: InternalAlignment(g204,g205)
    c: InternalAlignment(g206,g205)
    c: InternalAlignment(g207,g205)
    c: Block(g205)
    c: Block(g199)
    c: Coincident(g208,g205)
    c: Coincident(g208,g40)
    c: Coincident(g209,g40)
    c: Coincident(g209,g199)
    c: Coincident(g210,g199)
    c: Coincident(g210,g205)
    c: Vertical(g210)
    c: Weight(g211) = 1
    c: Equal(g211,g212)
    c: Equal(g211,g213)
    c: InternalAlignment(g211,g214)
    c: InternalAlignment(g212,g214)
    c: InternalAlignment(g213,g214)
    c: InternalAlignment(g215,g214)
    c: InternalAlignment(g216,g214)
    c: Weight(g217) = 1
    c: Equal(g217,g218)
    c: Equal(g217,g219)
    c: InternalAlignment(g217,g220)
    c: InternalAlignment(g218,g220)
    c: InternalAlignment(g219,g220)
    c: InternalAlignment(g221,g220)
    c: InternalAlignment(g222,g220)
    c: Block(g220)
    c: Block(g214)
    c: Coincident(g223,g214)
    c: Coincident(g223,g46)
    c: Coincident(g224,g46)
    c: Coincident(g224,g220)
    c: Coincident(g225,g220)
    c: Coincident(g225,g214)
    c: Vertical(g225)
    c: Horizontal(g226)
    c: Block(g226)
    c: Vertical(g227)
    c: Block(g227)
    c: Block(g228)
    c: Weight(g229) = 1
    c: Equal(g229,g230)
    c: Equal(g229,g231)
    c: InternalAlignment(g229,g232)
    c: InternalAlignment(g230,g232)
    c: InternalAlignment(g231,g232)
    c: InternalAlignment(g233,g232)
    c: InternalAlignment(g234,g232)
    c: Weight(g235) = 1
    c: Equal(g235,g236)
    c: Equal(g235,g237)
    c: InternalAlignment(g235,g238)
    c: InternalAlignment(g236,g238)
    c: InternalAlignment(g237,g238)
    c: InternalAlignment(g239,g238)
    c: InternalAlignment(g240,g238)
    c: Weight(g241) = 1
    c: Equal(g241,g242)
    c: Equal(g241,g243)
    c: InternalAlignment(g241,g244)
    c: InternalAlignment(g242,g244)
    c: InternalAlignment(g243,g244)
    c: InternalAlignment(g245,g244)
    c: InternalAlignment(g246,g244)
    c: Weight(g247) = 1
    c: Equal(g247,g248)
    c: Equal(g247,g249)
    c: InternalAlignment(g247,g250)
    c: InternalAlignment(g248,g250)
    c: InternalAlignment(g249,g250)
    c: InternalAlignment(g251,g250)
    c: InternalAlignment(g252,g250)
    c: Block(g232)
    c: Block(g238)
    c: Block(g244)
    c: Block(g250)
    c: Coincident(g253,g238)
    c: Coincident(g253,g232)
    c: Horizontal(g253)
    c: Block(g195)
    c: Weight(g254) = 1
    c: Equal(g254,g255)
    c: Equal(g254,g256)
    c: InternalAlignment(g254,g257)
    c: InternalAlignment(g255,g257)
    c: InternalAlignment(g256,g257)
    c: InternalAlignment(g258,g257)
    c: InternalAlignment(g259,g257)
    c: Weight(g260) = 1
    c: Equal(g260,g261)
    c: Equal(g260,g262)
    c: InternalAlignment(g260,g263)
    c: InternalAlignment(g261,g263)
    c: InternalAlignment(g262,g263)
    c: InternalAlignment(g264,g263)
    c: InternalAlignment(g265,g263)
    c: Block(g257)
    c: Block(g263)
    c: Coincident(g338,g257)
    c: Coincident(g266,g257)
    c: Coincident(g266,g263)
    c: Coincident(g267,g263)
    c: Vertical(g267)
    c: Weight(g268) = 1
    c: Equal(g268,g269)
    c: Equal(g268,g270)
    c: InternalAlignment(g268,g271)
    c: InternalAlignment(g269,g271)
    c: InternalAlignment(g270,g271)
    c: InternalAlignment(g272,g271)
    c: InternalAlignment(g273,g271)
    c: Weight(g274) = 1
    c: Equal(g274,g275)
    c: Equal(g274,g276)
    c: InternalAlignment(g274,g277)
    c: InternalAlignment(g275,g277)
    c: InternalAlignment(g276,g277)
    c: InternalAlignment(g278,g277)
    c: InternalAlignment(g279,g277)
    c: Weight(g280) = 1
    c: Equal(g280,g281)
    c: Equal(g280,g282)
    c: InternalAlignment(g280,g283)
    c: InternalAlignment(g281,g283)
    c: InternalAlignment(g282,g283)
    c: InternalAlignment(g284,g283)
    c: InternalAlignment(g285,g283)
    c: Block(g283)
    c: Block(g277)
    c: Block(g271)
    c: Coincident(g286,g277)
    c: Coincident(g286,g271)
    c: Coincident(g287,g271)
    c: Coincident(g287,g283)
    c: Vertical(g287)
    c: Coincident(g288,g283)
    c: Coincident(g288,g277)
    c: Horizontal(g288)
    c: Weight(g289) = 1
    c: Equal(g289,g290)
    c: InternalAlignment(g289,g291)
    c: InternalAlignment(g290,g291)
    c: InternalAlignment(g292,g291)
    c: InternalAlignment(g293,g291)
    c: Weight(g294) = 1
    c: Equal(g294,g295)
    c: Equal(g294,g296)
    c: InternalAlignment(g294,g297)
    c: InternalAlignment(g295,g297)
    c: InternalAlignment(g296,g297)
    c: InternalAlignment(g298,g297)
    c: InternalAlignment(g299,g297)
    c: Weight(g300) = 1
    c: Equal(g300,g301)
    c: Equal(g300,g302)
    c: InternalAlignment(g300,g303)
    c: InternalAlignment(g301,g303)
    c: InternalAlignment(g302,g303)
    c: InternalAlignment(g304,g303)
    c: InternalAlignment(g305,g303)
    c: Equal(g306,g307)
    c: Equal(g306,g308)
    c: InternalAlignment(g306,g309)
    c: InternalAlignment(g307,g309)
    c: InternalAlignment(g308,g309)
    c: InternalAlignment(g310,g309)
    c: InternalAlignment(g311,g309)
    c: Block(g297)
    c: Block(g303)
    c: Block(g309)
    c: Block(g291)
    c: Coincident(g312,g291)
    c: Coincident(g312,g297)
    c: Horizontal(g312)
    c: Coincident(g313,g297)
    c: Coincident(g313,g303)
    c: Vertical(g313)
    c: Coincident(g314,g303)
    c: Coincident(g314,g309)
    c: Horizontal(g314)
    c: Coincident(g315,g309)
    c: Coincident(g315,g291)
    c: Weight(g316) = 1
    c: Equal(g316,g317)
    c: Equal(g316,g318)
    c: InternalAlignment(g316,g319)
    c: InternalAlignment(g317,g319)
    c: InternalAlignment(g318,g319)
    c: InternalAlignment(g320,g319)
    c: InternalAlignment(g321,g319)
    c: Weight(g322) = 1
    c: Equal(g322,g323)
    c: Equal(g322,g324)
    c: InternalAlignment(g322,g325)
    c: InternalAlignment(g323,g325)
    c: InternalAlignment(g324,g325)
    c: InternalAlignment(g326,g325)
    c: InternalAlignment(g327,g325)
    c: Weight(g328) = 1
    c: Equal(g328,g329)
    c: Equal(g328,g330)
    c: InternalAlignment(g328,g331)
    c: InternalAlignment(g329,g331)
    c: InternalAlignment(g330,g331)
    c: InternalAlignment(g332,g331)
    c: InternalAlignment(g333,g331)
    c: Block(g331)
    c: Block(g325)
    c: Block(g319)
    c: Coincident(g334,g331)
    c: Coincident(g334,g325)
    c: Horizontal(g334)
    c: Coincident(g335,g325)
    c: Coincident(g335,g319)
    c: Vertical(g335)
    c: Coincident(g336,g319)
    c: Coincident(g336,g331)
    c: Block(g337)
    c: Coincident(g338,g337)
    c: Coincident(g267,g337)
    c: Horizontal(g339)
    c: Distance(g339) = 4
    c: Coincident(g339,g267)
    c: InternalAlignment(g340,g341)
    c: InternalAlignment(g342,g341)
    c: InternalAlignment(g343,g341)
    c: Block(g341)
    c: Coincident(g343,g339)
    c: Horizontal(g344)
    c: Distance(g344) = 4
    c: Coincident(g344,g337)
    c: Equal(g345,g346)
    c: Equal(g345,g347)
    c: InternalAlignment(g345,g348)
    c: InternalAlignment(g346,g348)
    c: InternalAlignment(g347,g348)
    c: InternalAlignment(g349,g348)
    c: InternalAlignment(g350,g348)
    c: Block(g348)
    c: Coincident(g350,g344)
FEATURE [Sketcher::SketchObject] Sketch001
  FullyConstrained = true
  MapMode = 4
  Placement = pos=(0,0,0) rot=(0.57735,0.57735,0.57735;2.0944rad)
  Support = -> [Sketch]
  sketch-geometry (46):
    g0: BSplineCurve PolesCount=3 KnotsCount=2 Degree=2 IsPeriodic=0
    g1: ArcOfCircle CenterX=73.1223 CenterY=-32.291 CenterZ=0 NormalX=0 NormalY=0 NormalZ=1 AngleXU=0 Radius=13 StartAngle=5.92268 EndAngle=9.06428
    g2: ArcOfCircle CenterX=66.7816 CenterY=-49.1439 CenterZ=0 NormalX=0 NormalY=0 NormalZ=1 AngleXU=0 Radius=13 StartAngle=2.78068 EndAngle=5.92131
    g3: ArcOfCircle CenterX=55.9263 CenterY=-78.1807 CenterZ=0 NormalX=0 NormalY=0 NormalZ=1 AngleXU=0 Radius=13 StartAngle=5.92268 EndAngle=9.06428
    g4: ArcOfCircle CenterX=49.5884 CenterY=-95.0342 CenterZ=0 NormalX=0 NormalY=0 NormalZ=1 AngleXU=0 Radius=13 StartAngle=2.78068 EndAngle=5.92131
    g5: ArcOfCircle CenterX=38.7206 CenterY=-124.067 CenterZ=0 NormalX=0 NormalY=0 NormalZ=1 AngleXU=0 Radius=13 StartAngle=5.92268 EndAngle=9.06428
    g6: ArcOfCircle CenterX=32.3875 CenterY=-140.92 CenterZ=0 NormalX=0 NormalY=0 NormalZ=1 AngleXU=0 Radius=13 StartAngle=2.78068 EndAngle=5.92131
    g7: ArcOfCircle CenterX=21.4715 CenterY=-169.934 CenterZ=0 NormalX=0 NormalY=0 NormalZ=1 AngleXU=0 Radius=13 StartAngle=5.92268 EndAngle=9.06428
    g8: ArcOfCircle CenterX=15.1336 CenterY=-186.787 CenterZ=0 NormalX=0 NormalY=0 NormalZ=1 AngleXU=0 Radius=13 StartAngle=2.78068 EndAngle=5.92131
    g9-g12: Circle x4 (B-spline internal-alignment scaffolding for g13; pole/knot coordinates omitted)
    g13: BSplineCurve PolesCount=4 KnotsCount=2 Degree=3 IsPeriodic=0
    g14: GeomPoint X=28.8094 Y=-19.0875 Z=0
    g15: GeomPoint X=47.0443 Y=-50.4712 Z=0
    g16: Circle CenterX=53.5586 CenterY=-23.2695 CenterZ=0 NormalX=0 NormalY=0 NormalZ=1 AngleXU=0 Radius=3.24518
    g17: Circle CenterX=-195.441 CenterY=-127.082 CenterZ=0 NormalX=0 NormalY=0 NormalZ=1 AngleXU=0 Radius=1
    g18: Circle CenterX=-8.24091 CenterY=-197.481 CenterZ=0 NormalX=0 NormalY=0 NormalZ=1 AngleXU=0 Radius=1
    g19: Circle CenterX=12.8789 CenterY=-141.321 CenterZ=0 NormalX=0 NormalY=0 NormalZ=1 AngleXU=0 Radius=1
    g20: BSplineCurve PolesCount=3 KnotsCount=2 Degree=2 IsPeriodic=0
    g21: GeomPoint X=-195.441 Y=-127.082 Z=0
    g22: GeomPoint X=12.8789 Y=-141.321 Z=0
    g23: Circle CenterX=-12.8016 CenterY=-179.036 CenterZ=0 NormalX=0 NormalY=0 NormalZ=1 AngleXU=0 Radius=10.5072
    g24: Circle CenterX=0.933922 CenterY=-166.43 CenterZ=0 NormalX=0 NormalY=0 NormalZ=1 AngleXU=0 Radius=3.26661
    g25: Circle CenterX=-33.5518 CenterY=-176.44 CenterZ=0 NormalX=0 NormalY=0 NormalZ=1 AngleXU=0 Radius=5.64388
    g26: Circle CenterX=-47.2366 CenterY=-173.859 CenterZ=0 NormalX=0 NormalY=0 NormalZ=1 AngleXU=0 Radius=3.01653
    g27: Circle CenterX=-56.2595 CenterY=-171.456 CenterZ=0 NormalX=0 NormalY=0 NormalZ=1 AngleXU=0 Radius=2.12826
    g28: ArcOfCircle CenterX=51.2151 CenterY=-198.473 CenterZ=0 NormalX=0 NormalY=0 NormalZ=1 AngleXU=0 Radius=20 StartAngle=2.78189 EndAngle=4.35269
    g29: LineSegment StartX=32.4951 StartY=-191.433 StartZ=0 EndX=94.6578 EndY=-26.1352 EndZ=0
    g30: LineSegment StartX=43.1192 StartY=-220.001 StartZ=0 EndX=-196.497 EndY=-129.89 EndZ=0
    g31: LineSegment StartX=43.1192 StartY=-220.001 StartZ=0 EndX=44.1752 EndY=-217.193 EndZ=0
    g32: LineSegment StartX=117.223 StartY=-19.0875 StartZ=0 EndX=117.223 EndY=-16.0875 EndZ=0
    g33: LineSegment StartX=117.223 StartY=-16.0875 StartZ=0 EndX=17.2232 EndY=-16.0875 EndZ=0
    g34: LineSegment StartX=17.2232 StartY=-16.0875 StartZ=0 EndX=17.2232 EndY=-19.0875 EndZ=0
    g35: LineSegment StartX=28.8094 StartY=-19.0875 StartZ=0 EndX=17.2232 EndY=-19.0875 EndZ=0
    g36: LineSegment StartX=47.0443 StartY=-50.4712 StartZ=0 EndX=12.8789 EndY=-141.321 EndZ=0
    g37: LineSegment StartX=-195.441 StartY=-127.082 StartZ=0 EndX=-196.497 EndY=-129.89 EndZ=0
    g38: LineSegment StartX=85.2866 StartY=-36.8766 StartZ=0 EndX=78.9396 EndY=-53.7463 EndZ=0
    g39: LineSegment StartX=60.9579 StartY=-27.7053 StartZ=0 EndX=54.6191 EndY=-44.5532 EndZ=0
    g40: LineSegment StartX=68.0907 StartY=-82.7664 StartZ=0 EndX=61.7465 EndY=-99.6365 EndZ=0
    g41: LineSegment StartX=43.7619 StartY=-73.595 StartZ=0 EndX=37.426 EndY=-90.4435 EndZ=0
    g42: LineSegment StartX=50.885 StartY=-128.652 StartZ=0 EndX=44.5456 EndY=-145.522 EndZ=0
    g43: LineSegment StartX=26.5562 StartY=-119.481 StartZ=0 EndX=20.2251 EndY=-136.329 EndZ=0
    g44: LineSegment StartX=9.3071 StartY=-165.349 StartZ=0 EndX=2.97115 EndY=-182.197 EndZ=0
    g45: LineSegment StartX=33.6358 StartY=-174.52 StartZ=0 EndX=27.2917 EndY=-191.39 EndZ=0
  constraints (71):
    c: Block(g0)
    c: Block(g1)
    c: Block(g2)
    c: Block(g4)
    c: Block(g3)
    c: Block(g6)
    c: Block(g5)
    c: Block(g8)
    c: Block(g7)
    c: Weight(g9) = 1
    c: Equal(g9,g10)
    c: Equal(g9,g11)
    c: Equal(g9,g12)
    c: InternalAlignment(g9-g12 -> g13) x4
    c: InternalAlignment(g14,g13)
    c: InternalAlignment(g15,g13)
    c: Block(g16)
    c: Weight(g17) = 1
    c: Equal(g17,g18)
    c: Equal(g17,g19)
    c: InternalAlignment(g17,g20)
    c: InternalAlignment(g18,g20)
    c: InternalAlignment(g19,g20)
    c: InternalAlignment(g21,g20)
    c: InternalAlignment(g22,g20)
    c: Block(g20)
    c: Block(g23)
    c: Block(g24)
    c: Block(g25)
    c: Block(g26)
    c: Block(g27)
    c: Block(g28)
    c: Coincident(g29,g28)
    c: Coincident(g29,g0)
    c: Block(g13)
    c: Coincident(g31,g30)
    c: Coincident(g31,g28)
    c: Block(g31)
    c: Coincident(g32,g0)
    c: Vertical(g32)
    c: Coincident(g33,g32)
    c: Horizontal(g33)
    c: Coincident(g34,g33)
    c: Vertical(g34)
    c: Block(g33)
    c: Coincident(g35,g13)
    c: Coincident(g35,g34)
    c: Horizontal(g35)
    c: Coincident(g36,g13)
    c: Coincident(g36,g20)
    c: Coincident(g37,g20)
    c: Coincident(g37,g30)
    c: Block(g30)
    c: Coincident(g38,g1)
    c: Coincident(g38,g2)
    c: Coincident(g39,g1)
    c: Coincident(g39,g2)
    c: Coincident(g40,g3)
    c: Coincident(g40,g4)
    c: Coincident(g41,g3)
    c: Coincident(g41,g4)
    c: Coincident(g42,g5)
    c: Coincident(g42,g6)
    c: Coincident(g43,g5)
    c: Coincident(g43,g6)
    c: Coincident(g44,g7)
    c: Coincident(g44,g8)
    c: Coincident(g45,g7)
    c: Coincident(g45,g8)
    c: Distance(g30) = 256
    c: Distance(g33) = 100
FEATURE [Part::Extrusion] Extrude002
  Base = -> Sketch001
  Dir = (1,0,0)
  DirMode = 2
  FaceMakerClass = Part::FaceMakerBullseye
  LengthFwd = 8
  LengthRev = 0
  Solid = true
  Symmetric = false
FEATURE [Sketcher::SketchObject] Sketch002
  FullyConstrained = true
  sketch-geometry (20):
    g0: LineSegment StartX=-2.77179 StartY=-200.304 StartZ=0 EndX=5.22821 EndY=-200.304 EndZ=0
    g1: LineSegment StartX=5.22821 StartY=-200.304 StartZ=0 EndX=5.22821 EndY=-197.304 EndZ=0
    g2: LineSegment StartX=-2.77179 StartY=-200.304 StartZ=0 EndX=-2.77179 EndY=-197.304 EndZ=0
    g3: LineSegment StartX=5.22821 StartY=-197.304 StartZ=0 EndX=8.22821 EndY=-197.304 EndZ=0
    g4: LineSegment StartX=-2.77179 StartY=-197.304 StartZ=0 EndX=-5.77179 EndY=-197.304 EndZ=0
    g5: LineSegment StartX=19.2282 StartY=-203.304 StartZ=0 EndX=19.2282 EndY=-206.304 EndZ=0
    g6: LineSegment StartX=-16.7718 StartY=-203.304 StartZ=0 EndX=-16.7718 EndY=-206.304 EndZ=0
    g7: LineSegment StartX=-16.7718 StartY=-206.304 StartZ=0 EndX=19.2282 EndY=-206.304 EndZ=0
    g8: Circle CenterX=-16.7718 CenterY=-203.304 CenterZ=0 NormalX=0 NormalY=0 NormalZ=1 AngleXU=0 Radius=1
    g9: Circle CenterX=-5.77179 CenterY=-203.304 CenterZ=0 NormalX=0 NormalY=0 NormalZ=1 AngleXU=0 Radius=1
    g10: Circle CenterX=-5.77179 CenterY=-197.304 CenterZ=0 NormalX=0 NormalY=0 NormalZ=1 AngleXU=0 Radius=1
    g11: BSplineCurve PolesCount=3 KnotsCount=2 Degree=2 IsPeriodic=0
    g12: GeomPoint X=-16.7718 Y=-203.304 Z=0
    g13: GeomPoint X=-5.77179 Y=-197.304 Z=0
    g14: Circle CenterX=19.2282 CenterY=-203.304 CenterZ=0 NormalX=0 NormalY=0 NormalZ=1 AngleXU=0 Radius=1
    g15: Circle CenterX=8.22821 CenterY=-203.304 CenterZ=0 NormalX=0 NormalY=0 NormalZ=1 AngleXU=0 Radius=1
    g16: Circle CenterX=8.22821 CenterY=-197.304 CenterZ=0 NormalX=0 NormalY=0 NormalZ=1 AngleXU=0 Radius=1
    g17: BSplineCurve PolesCount=3 KnotsCount=2 Degree=2 IsPeriodic=0
    g18: GeomPoint X=19.2282 Y=-203.304 Z=0
    g19: GeomPoint X=8.22821 Y=-197.304 Z=0
  constraints (41):
    c: Horizontal(g0)
    c: Distance(g0) = 8
    c: Coincident(g1,g0)
    c: Vertical(g1)
    c: Distance(g1) = 3
    c: Coincident(g2,g0)
    c: Vertical(g2)
    c: Distance(g2) = 3
    c: Coincident(g3,g1)
    c: Horizontal(g3)
    c: Distance(g3) = 3
    c: Coincident(g4,g2)
    c: Horizontal(g4)
    c: Distance(g4) = 3
    c: Vertical(g5)
    c: Vertical(g6)
    c: Coincident(g7,g6)
    c: Coincident(g7,g5)
    c: Weight(g8) = 1
    c: Equal(g8,g9)
    c: Equal(g8,g10)
    c: Coincident(g11,g4)
    c: InternalAlignment(g8,g11)
    c: InternalAlignment(g9,g11)
    c: InternalAlignment(g10,g11)
    c: InternalAlignment(g12,g11)
    c: InternalAlignment(g13,g11)
    c: Coincident(g17,g5)
    c: Weight(g14) = 1
    c: Equal(g14,g15)
    c: Equal(g14,g16)
    c: Coincident(g17,g3)
    c: InternalAlignment(g14,g17)
    c: InternalAlignment(g15,g17)
    c: InternalAlignment(g16,g17)
    c: InternalAlignment(g18,g17)
    c: InternalAlignment(g19,g17)
    c: Block(g7)
    c: Block(g17)
    c: Block(g11)
    c: Block(g6)
FEATURE [Part::Extrusion] Extrude003
  Base = -> Sketch002
  Dir = (0,0,1)
  DirMode = 2
  FaceMakerClass = Part::FaceMakerBullseye
  LengthFwd = 260
  LengthRev = 0
  Solid = true
  Symmetric = false
FEATURE [Part::Extrusion] Extrude
  Base = -> Sketch
  Dir = (0,0,1)
  DirMode = 2
  FaceMakerClass = Part::FaceMakerBullseye
  LengthFwd = 14
  LengthRev = 0
  Solid = true
  Symmetric = false
